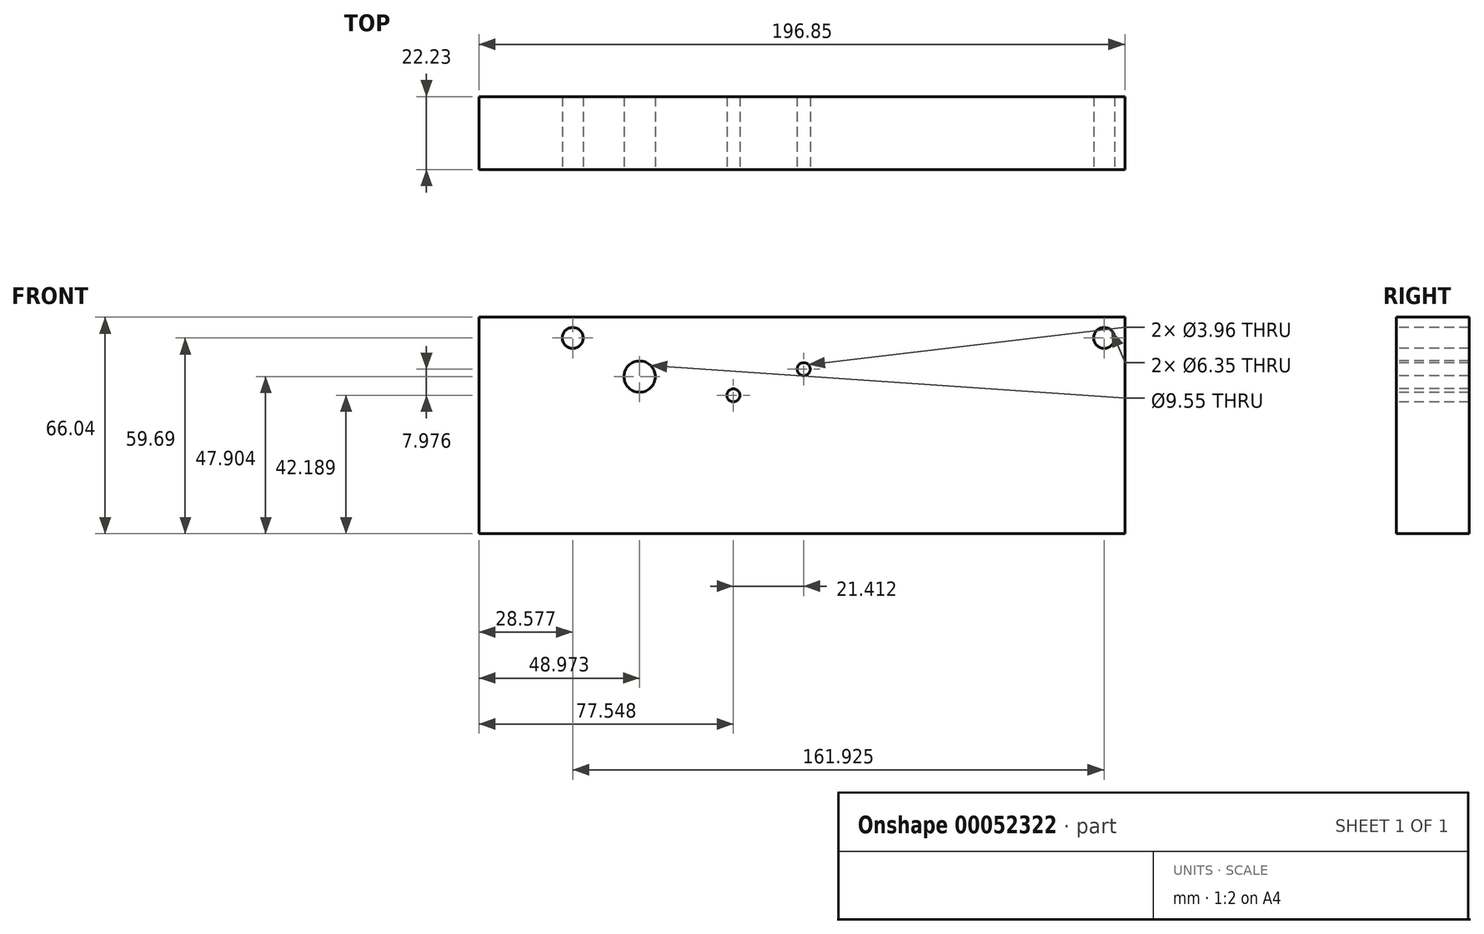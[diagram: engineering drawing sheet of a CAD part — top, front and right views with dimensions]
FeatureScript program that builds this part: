
annotation { "Feature Type Name" : "Feature", "Feature Type Description" : "" }
export const myFeature = defineFeature(function(context is Context, id is Id, definition is map)
    precondition{}
    {
        {
            var Q0;
            Q0=qCreatedBy(makeId("Top.planeOp"),FACE);
            var sketch = newSketch(context, id + "F0", { "sketchPlane" : qUnion([Q0])});
            skLineSegment(sketch, "E0.bottom", {"start": v(-98.96, 10.9) * mm, "end": v(97.9, 10.9) * mm});
            skLineSegment(sketch, "E0.top", {"start": v(-98.96, -11.32) * mm, "end": v(97.9, -11.32) * mm});
            skLineSegment(sketch, "E0.left", {"start": v(-98.96, 10.9) * mm, "end": v(-98.96, -11.32) * mm});
            skLineSegment(sketch, "E0.right", {"start": v(97.9, 10.9) * mm, "end": v(97.9, -11.32) * mm});
            skSolve(sketch);
        }
        {
            var Q0;
            Q0=makeQuery(id+"F0.imprint","IMPRINT",FACE,{"disambiguationData":[TD([[makeQuery(id+"F0.imprint","IMPRINT",EDGE,{"derivedFrom":sQuery(id+"F0.wireOp",EDGE,"E0.bottom")}),-1.0]])]});
            extrude(context, id + "F1", {"entities" : qUnion([Q0]), "oppositeDirection" : true, "depth" : 66.04 * mm});
        }
        {
            var Q0;
            Q0=makeQuery(id+"F1.opExtrude","SWEPT_FACE",FACE,{"disambiguationData":[OSD([sQuery(id+"F0.wireOp",EDGE,"E0.top")])]});
            var sketch = newSketch(context, id + "F2", { "sketchPlane" : qUnion([Q0])});
            skCircle(sketch, "E1", {"center": v(91.54, -6.35) * mm, "radius": 3.18 * mm});
            skCircle(sketch, "E2", {"center": v(-70.38, -6.35) * mm, "radius": 3.18 * mm});
            skCircle(sketch, "E3", {"center": v(-49.99, -18.14) * mm, "radius": 4.78 * mm});
            skCircle(sketch, "E4", {"center": v(-21.41, -23.85) * mm, "radius": 1.98 * mm});
            skCircle(sketch, "E5", {"center": v(0, -15.87) * mm, "radius": 1.98 * mm});
            skSolve(sketch);
        }
        {
            var Q0;
            Q0=qSketchRegion(id+"F2",true);
            extrude(context, id + "F3", {"entities" : qUnion([Q0]), "operationType" : NewBodyOperationType.REMOVE, "endBound" : BoundingType.THROUGH_ALL, "oppositeDirection" : true, "depth" : 25.4 * mm});
        }
    });
